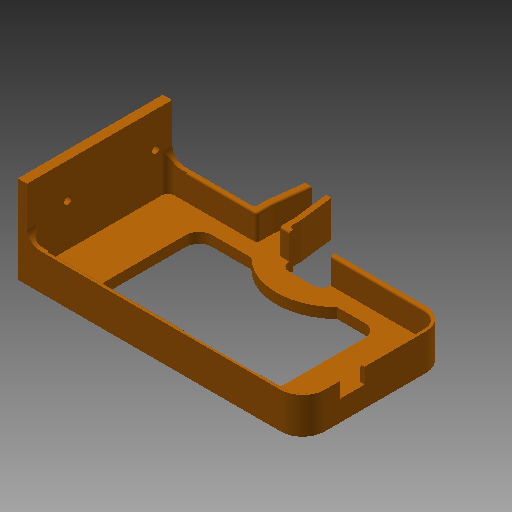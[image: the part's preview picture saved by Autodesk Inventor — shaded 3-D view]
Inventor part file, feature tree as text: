
AUTODESK INVENTOR PART (.ipt)
format: ipt  version: 2019 (Build 230136000, 136)  size: 465,920 bytes
history: native  units: in
note: dims shown in document units (in); Inventor stores cm internally (conversion verified against a paired STEP export)
features: sketch x20, extrude x19, fillet x11, thicken_offset x4, projected_geometry x4, hole x1
ambient origin geometry x8: Origin, YZ Plane, XZ Plane, XY Plane, X Axis, Y Axis, Z Axis, Center Point
bodies: Solid1 (feature_tree)
feature tree (59):
  extrude  "Extrusion1"  Depth=2.655in
  extrude  "Extrusion2"  Depth=0.5in TaperAngle=0.0deg
  fillet  "Fillet1"  Radius=0.2in
  fillet  "Fillet2"  Radius=0.3in
  extrude  "Extrusion3"  Depth=0.42in
  extrude  "Extrusion4"  Depth=0.125in
  extrude  "Extrusion5"  Depth=0.125in
  fillet  "Fillet3"  Radius=0.125in
  fillet  "Fillet4"  Radius=0.125in
  fillet  "Fillet5"  Radius=0.125in
  extrude  "Extrusion6"  Depth=0.125in TaperAngle=0.0deg
  fillet  "Fillet6"  Radius=0.06in
  extrude  "Extrusion8"  Depth=0.25in
  fillet  "Fillet7"  Radius=0.25in
  extrude  "Extrusion10"  TaperAngle=0.0deg  [1 undecoded]
  extrude  "Extrusion11"  Depth=1.0in TaperAngle=0.0deg
  extrude  "Extrusion13"  Depth=1.1887in
  thicken_offset  "Thicken1"
  extrude  "Extrusion14"  Depth=1.932in
  sketch  "Sketch15"  dims[d57=0.25in d58=1.0in d59=0.0in]
  fillet  "Fillet10"  Radius=0.9in
  extrude  "Extrusion17"  Depth=0.3in
  fillet  "Fillet11"  Radius=0.3in
  thicken_offset  "Thicken2"
  thicken_offset  "Thicken3"
  thicken_offset  "Thicken4"
  extrude  "Extrusion18"  Depth=0.25in TaperAngle=0.0deg
  extrude  "Extrusion19"  Depth=0.48in
  extrude  "Extrusion20"  Depth=0.3in TaperAngle=0.0deg
  extrude  "Extrusion21"  TaperAngle=0.0deg  [1 undecoded]
  extrude  "Extrusion22"  Depth=0.875in
  extrude  "Extrusion23"  Depth=0.04in
  fillet  "Fillet12"  Radius=1.0in
  fillet  "Fillet13"  Radius=0.5in
  hole  "Hole1"  [1 undecoded]
  extrude  "Extrusion12"  Depth=0.25in
  sketch  "Sketch1"  dims[d0=5.265in d1=2.655in]
  sketch  "Sketch2"  dims[d2=0.08in d3=0.5in d4=0.0in d5=0.2in d6=0.0in d7=0.3in]
  sketch  "Sketch3"  dims[d8=0.425in d9=0.42in]
  sketch  "Sketch4"  dims[d10=0.125in d11=0.0in d14=0.2275in]
  sketch  "Sketch5"  dims[d15=0.9in d17=0.125in d18=0.125in d19=0.125in d20=0.125in]
  sketch  "Sketch6"  dims[d21=0.0in d22=0.0in d23=0.125in d24=0.0in d25=0.06in]
  sketch  "Sketch8"  dims[d26=0.06in d27=0.04in d29=0.25in]
  sketch  "Sketch10"  dims[d30=2.75in d31=0.0in d32=0.0in]
  sketch  "Sketch11"  dims[d33=0.16in d43=1.0in d44=0.0in]
  sketch  "Sketch12"  dims[d45=1.1887in d46=1.1887in]
  sketch  "Sketch13"  dims[d47=0.2549in d50=1.932in d53=0.9in]
  sketch  "Sketch14"  dims[d54=0.9in d55=0.3in d56=0.3in]
  projected_geometry  "Projected Loop1"
  projected_geometry  "Projected Loop2"
  projected_geometry  "Projected Loop3"
  sketch  "Sketch17"  dims[d61=0.8in d62=0.48in]
  sketch  "Sketch18"  dims[d63=0.88in d64=0.3in d65=0.0in]
  sketch  "Sketch19"  dims[d66=2.0in d67=0.0in d72=0.0in]
  sketch  "Sketch20"  dims[d73=0.0in d74=0.875in]
  sketch  "Sketch21"  dims[d75=1.0in d77=0.04in d78=1.0in d79=0.0in d80=0.5in]
  sketch  "Sketch22"  dims[d81=0.5in d82=0.1in d83=0.0in]
  sketch  "Sketch23"  dims[d88=0.18in d89=0.14in d92=0.1in d93=0.625in d94=1.25in d95=0.0in d96=0.0in d97=0.125in d98=0.375in d99=0.375in d100=0.55in d101=0.55in d102=0.125in d103=0.125in d104=1.0in d105=0.0in d106=1.0in d107=0.0in d108=1.0in d109=0.0in d110=1.0in d111=0.0in d112=1.0in d113=0.0in d114=1.0in d115=0.0in d116=0.25in d117=0.125in d118=0.678in d119=0.678in d120=0.32in d121=2.026in d122=0.14in d123=0.75in d124=0.375in d125=0.25in d126=0.5635in d127=1.0in d128=0.8108in]
  projected_geometry  "Projected Loop4"
note: 3 required parameter values undecoded (feature->parameter linkage not recoverable at this tier; creation-order binding heuristic only, values carry confidence <= 0.55)
